# Revit family: Plumbing Fixture-Grease_Interseptor_Mifab_MI-SAND-OIL
name_source: partatom
category: Plumbing Fixtures
revit_build: Autodesk Revit Structure 2013 (Build: 20120221_2030(x64)
units: mm (PartAtom-declared; Revit-internal decimal feet)

## types (12) — shared parameters
Assembly Code = D2090300
Description = Sand and Oil Interceptor
Floor Drain Material = Paint - Sherwin Williams Paint - #952C2A - Bellwood Red
Manufacturer = MIFAB
URL = www.mifab.com
zero-valued in all types: Default Elevation, WFU

## per-type parameters (varying)
| type | A | B | C | D | E | F | G | Standard Inlet And Outlet Radii | Water Capacity |
| MI-SO-0 | 42 " | 28 " | 6 " | 26 " | 32 " | 4 " | 19 " | 2 " | 108.9 Gallons |
| MI-SO-1 | 55 " | 37 " | 8 " | 26 " | 34 " | 4 " | 19 " | 2 " | 192.7 Gallons |
| MI-SO-2 | 58 " | 38 " | 8 " | 28 " | 36 " | 4 " | 21 " | 2 " | 226.9 Gallons |
| MI-SO-3 | 61 " | 39 " | 8 " | 28 " | 36 " | 4 " | 23 " | 2 " | 264.6 Gallons |
| MI-SO-4 | 70 " | 44 " | 10 " | 34 " | 44 " | 4 " | 27 " | 2 " | 395.6 Gallons |
| MI-SO-5 | 75 " | 46 " | 10 " | 38 " | 48 " | 4 " | 31 " | 2 " | 500.6 Gallons |
| MI-SO-6 | 77 " | 49 " | 12 " | 40 " | 52 " | 6 " | 32 " | 3 " | 579.7 Gallons |
| MI-SO-7* | 80 " | 51 " | 12 " | 40 " | 52 " | 6 " | 36 " | 3 " | 612.2 Gallons |
| MI-SO-8* | 84 " | 56 " | 14 " | 44 " | 58 " | 6 " | 46 " | 3 " | 785.9 Gallons |
| MI-SO-9* | 92 " | 61 " | 14 " | 54 " | 68 " | 6 " | 46 " | 3 " | 1172.3 Gallons |
| MI-SO-10* | 102 " | 74 " | 14 " | 62 " | 76 " | 8 " | 53 " | 4 " | 1807.8 Gallons |
| MI-SO-11* | 108 " | 76 " | 14 " | 66 " | 80 " | 8 " | 57 " | 4 " | 2105.3 Gallons |

note: column(s) folded — value = type name in every type: Model

## geometry (parser evidence)
native form markers: Blend x3, Sweep x1
no freeform markers — native parametric forms only
